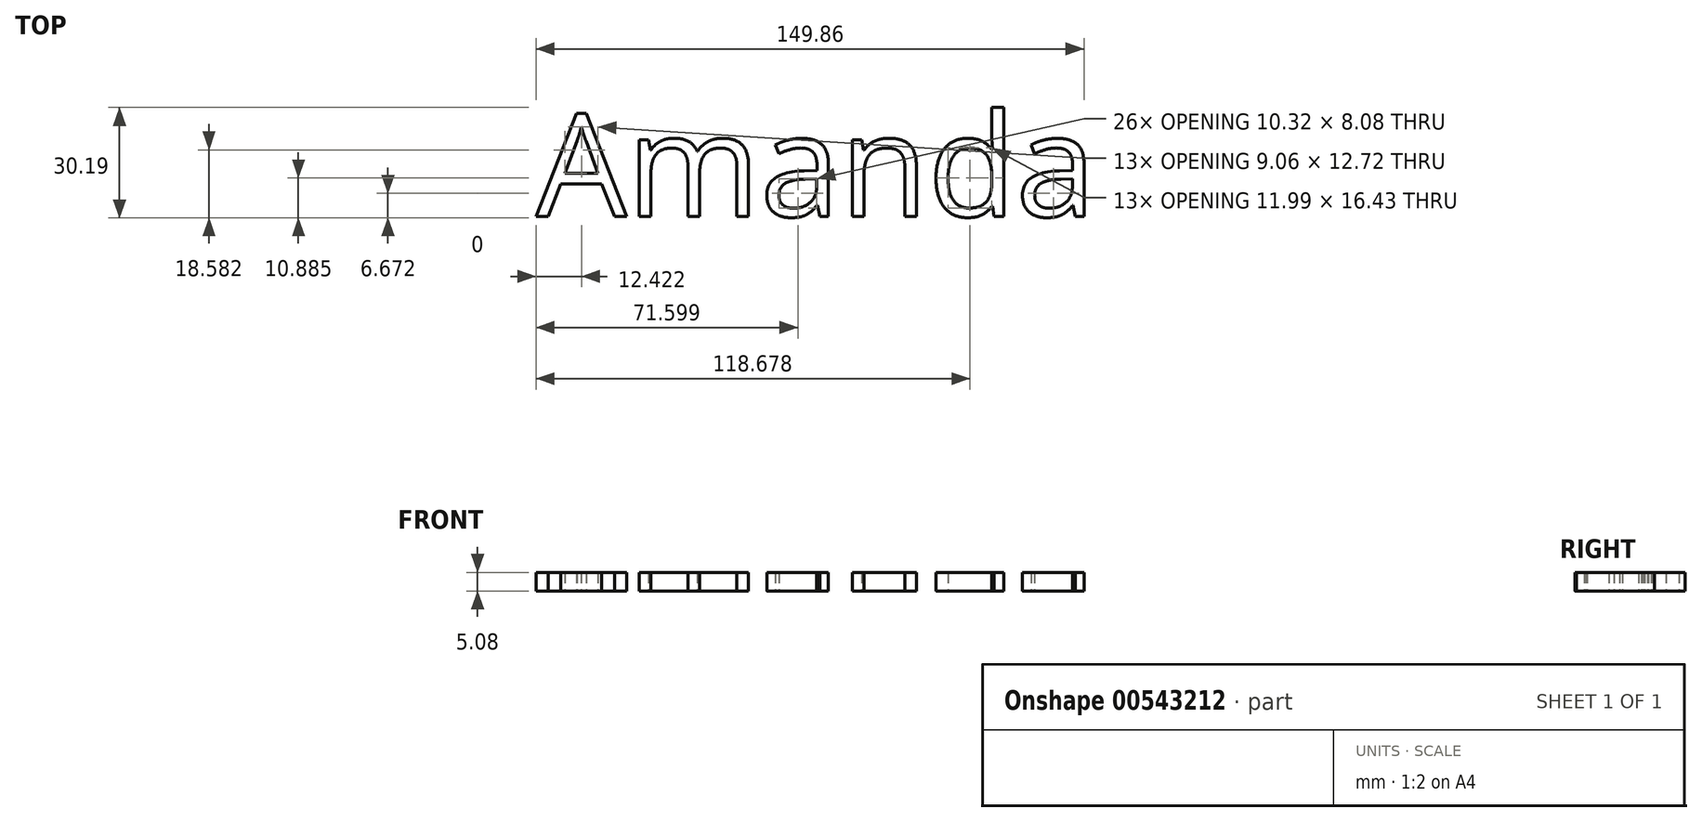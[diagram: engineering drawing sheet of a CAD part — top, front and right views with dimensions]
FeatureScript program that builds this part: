
annotation { "Feature Type Name" : "Feature", "Feature Type Description" : "" }
export const myFeature = defineFeature(function(context is Context, id is Id, definition is map)
    precondition{}
    {
        {
            var Q0;
            Q0=qCreatedBy(makeId("Top.planeOp"),FACE);
            var sketch = newSketch(context, id + "F0", { "sketchPlane" : qUnion([Q0])});
            skText(sketch, "E0", { "text": "Amanda\n", "fontName": "OpenSans-Regular.ttf"});
            const initialGuessF0  = {"E0": [-0.074, -0.0137, 1, 0, 0.02824]};
            skSetInitialGuess(sketch, initialGuessF0);
            skSolve(sketch);
        }
        {
            var Q0;
            Q0 = qSketchRegion(id + "F0", true);
            extrude(context, id + "F1", {"entities" : qUnion([Q0]), "depth" : 5.08 * mm, "offsetDistance" : 25.4 * mm});
        }
    });
